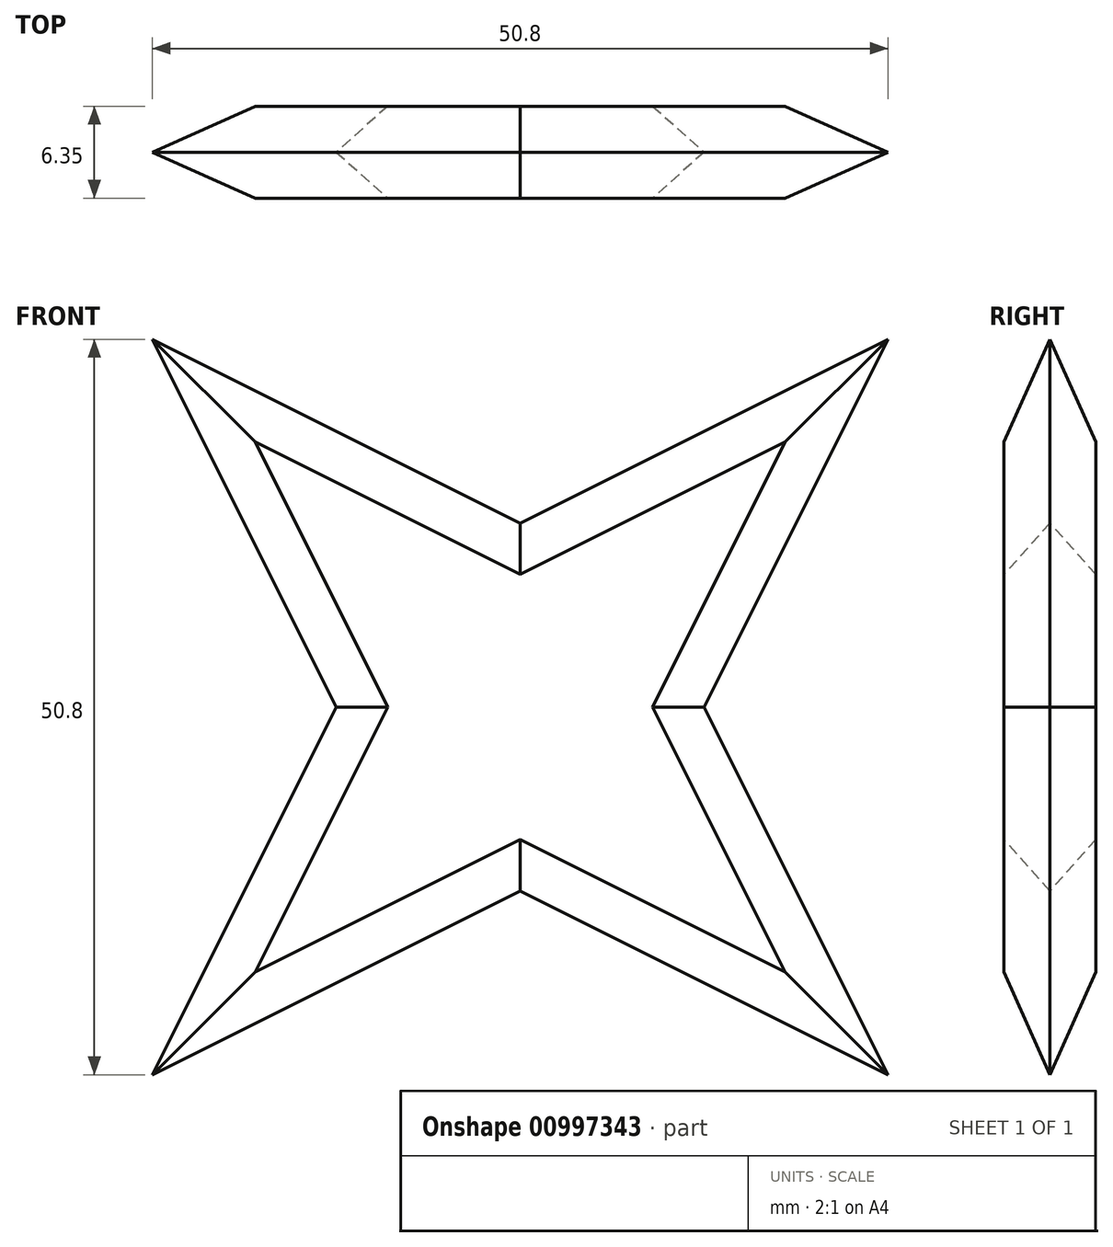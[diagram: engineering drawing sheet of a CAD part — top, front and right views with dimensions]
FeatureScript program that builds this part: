
annotation { "Feature Type Name" : "Feature", "Feature Type Description" : "" }
export const myFeature = defineFeature(function(context is Context, id is Id, definition is map)
    precondition{}
    {
        {
            var Q0;
            Q0=qCreatedBy(makeId("Front.planeOp"),FACE);
            var sketch = newSketch(context, id + "F0", { "sketchPlane" : qUnion([Q0])});
            skPoint(sketch, "E0.middle", {"position": v(0, 0) * mm});
            skPoint(sketch, "E1.middle", {"position": v(25.4, 25.4) * mm});
            skLineSegment(sketch, "E2", {"start": v(-25.4, 25.4) * mm, "end": v(0, 12.7) * mm});
            skLineSegment(sketch, "E3", {"start": v(0, 12.7) * mm, "end": v(25.4, 25.4) * mm});
            skLineSegment(sketch, "E4", {"start": v(25.4, 25.4) * mm, "end": v(12.7, 0) * mm});
            skLineSegment(sketch, "E5", {"start": v(12.7, 0) * mm, "end": v(25.4, -25.4) * mm});
            skLineSegment(sketch, "E6", {"start": v(25.4, -25.4) * mm, "end": v(0, -12.7) * mm});
            skLineSegment(sketch, "E7", {"start": v(0, -12.7) * mm, "end": v(-25.4, -25.4) * mm});
            skLineSegment(sketch, "E8", {"start": v(-25.4, 25.4) * mm, "end": v(-12.7, 0) * mm});
            skLineSegment(sketch, "E9", {"start": v(-12.7, 0) * mm, "end": v(-25.4, -25.4) * mm});
            skSolve(sketch);
        }
        {
            var Q0;
            Q0=makeQuery(id+"F0.imprint","IMPRINT",FACE,{"disambiguationData":[TD([[makeQuery(id+"F0.imprint","IMPRINT",EDGE,{"derivedFrom":sQuery(id+"F0.wireOp",EDGE,"E2")}),-1.0]])]});
            extrude(context, id + "F1", {"entities" : qUnion([Q0]), "depth" : 6.35 * mm, "offsetDistance" : 25.4 * mm});
        }
        {
            var Q0;
            Q0=makeQuery(id+"F1.opExtrude","CAP_EDGE",EDGE,{"disambiguationData":[OSD([sQuery(id+"F0.wireOp",EDGE,"E8")])],"isStart":false});
            var Q1;
            Q1=makeQuery(id+"F1.opExtrude","CAP_EDGE",EDGE,{"disambiguationData":[OSD([sQuery(id+"F0.wireOp",EDGE,"E2")])],"isStart":false});
            var Q2;
            Q2=makeQuery(id+"F1.opExtrude","CAP_EDGE",EDGE,{"disambiguationData":[OSD([sQuery(id+"F0.wireOp",EDGE,"E6")])],"isStart":false});
            var Q3;
            Q3=makeQuery(id+"F1.opExtrude","CAP_EDGE",EDGE,{"disambiguationData":[OSD([sQuery(id+"F0.wireOp",EDGE,"E5")])],"isStart":false});
            var Q4;
            Q4=makeQuery(id+"F1.opExtrude","CAP_EDGE",EDGE,{"disambiguationData":[OSD([sQuery(id+"F0.wireOp",EDGE,"E4")])],"isStart":false});
            var Q5;
            Q5=makeQuery(id+"F1.opExtrude","CAP_EDGE",EDGE,{"disambiguationData":[OSD([sQuery(id+"F0.wireOp",EDGE,"E3")])],"isStart":false});
            var Q6;
            Q6=makeQuery(id+"F1.opExtrude","CAP_EDGE",EDGE,{"disambiguationData":[OSD([sQuery(id+"F0.wireOp",EDGE,"E9")])],"isStart":false});
            var Q7;
            Q7=makeQuery(id+"F1.opExtrude","CAP_EDGE",EDGE,{"disambiguationData":[OSD([sQuery(id+"F0.wireOp",EDGE,"E7")])],"isStart":false});
            chamfer(context, id + "F2", {"entities" : qUnion([Q0, Q1, Q2, Q3, Q4, Q5, Q6, Q7]), "width" : 3.17 * mm, "tangentPropagation" : true});
        }
        {
            var Q0;
            Q0=makeQuery(id+"F1.opExtrude","CAP_EDGE",EDGE,{"disambiguationData":[OSD([sQuery(id+"F0.wireOp",EDGE,"E9")])],"isStart":true});
            var Q1;
            Q1=makeQuery(id+"F1.opExtrude","CAP_EDGE",EDGE,{"disambiguationData":[OSD([sQuery(id+"F0.wireOp",EDGE,"E7")])],"isStart":true});
            var Q2;
            Q2=makeQuery(id+"F1.opExtrude","CAP_EDGE",EDGE,{"disambiguationData":[OSD([sQuery(id+"F0.wireOp",EDGE,"E6")])],"isStart":true});
            var Q3;
            Q3=makeQuery(id+"F1.opExtrude","CAP_EDGE",EDGE,{"disambiguationData":[OSD([sQuery(id+"F0.wireOp",EDGE,"E5")])],"isStart":true});
            var Q4;
            Q4=makeQuery(id+"F1.opExtrude","CAP_EDGE",EDGE,{"disambiguationData":[OSD([sQuery(id+"F0.wireOp",EDGE,"E4")])],"isStart":true});
            var Q5;
            Q5=makeQuery(id+"F1.opExtrude","CAP_EDGE",EDGE,{"disambiguationData":[OSD([sQuery(id+"F0.wireOp",EDGE,"E3")])],"isStart":true});
            var Q6;
            Q6=makeQuery(id+"F1.opExtrude","CAP_EDGE",EDGE,{"disambiguationData":[OSD([sQuery(id+"F0.wireOp",EDGE,"E2")])],"isStart":true});
            var Q7;
            Q7=makeQuery(id+"F1.opExtrude","CAP_EDGE",EDGE,{"disambiguationData":[OSD([sQuery(id+"F0.wireOp",EDGE,"E8")])],"isStart":true});
            chamfer(context, id + "F3", {"entities" : qUnion([Q0, Q1, Q2, Q3, Q4, Q5, Q6, Q7]), "width" : 3.17 * mm, "tangentPropagation" : true});
        }
    });
